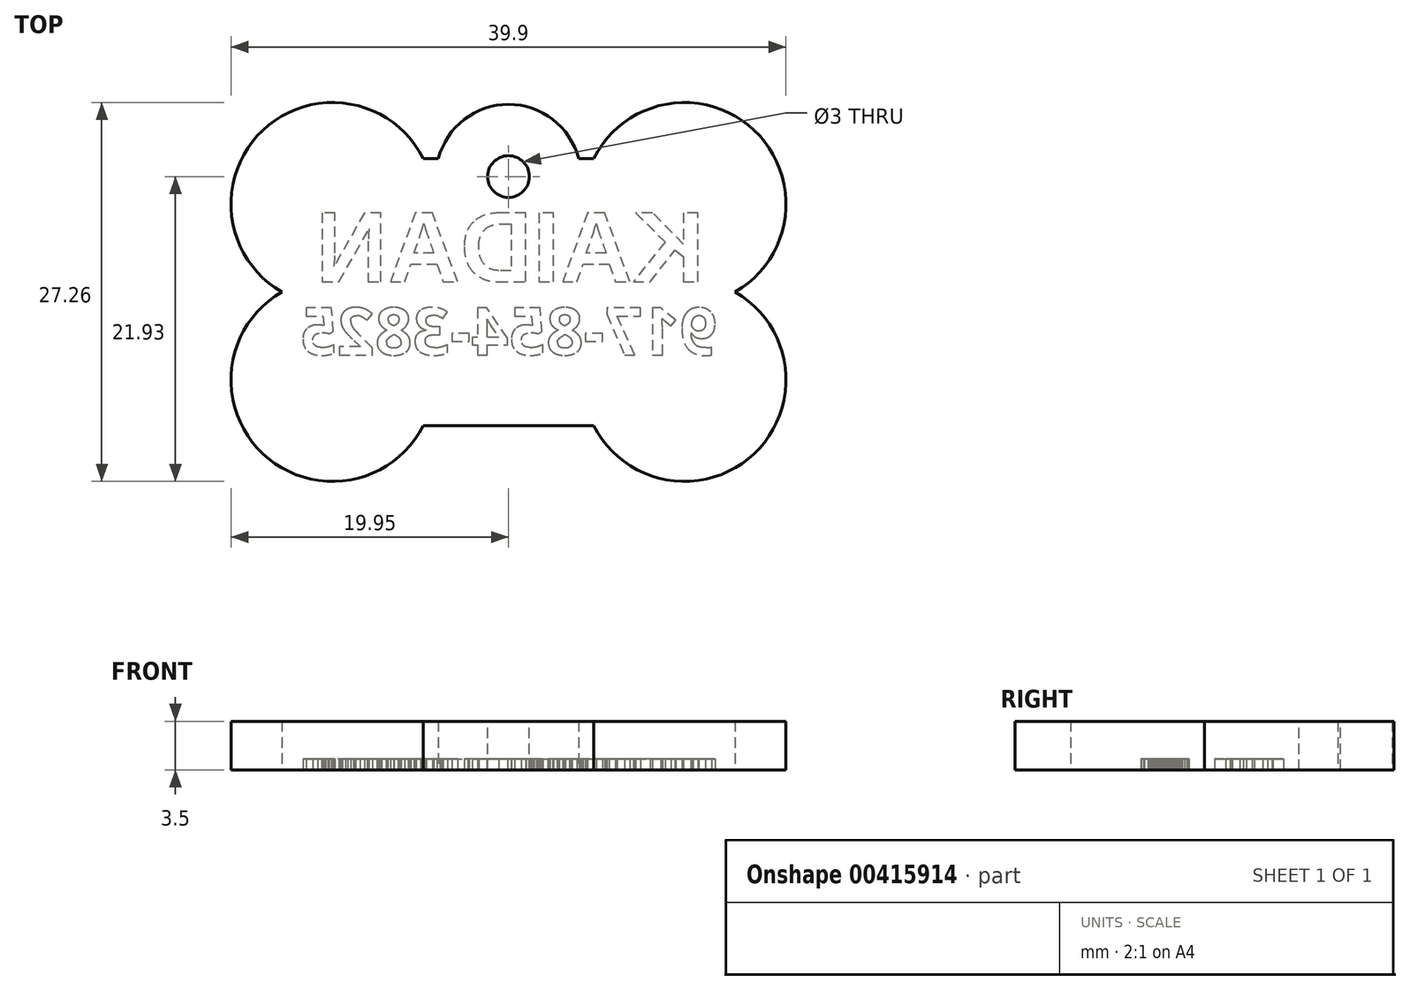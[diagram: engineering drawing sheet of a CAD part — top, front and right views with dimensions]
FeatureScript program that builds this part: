
annotation { "Feature Type Name" : "Feature", "Feature Type Description" : "" }
export const myFeature = defineFeature(function(context is Context, id is Id, definition is map)
    precondition{}
    {
        {
            var Q0;
            Q0=qCreatedBy(makeId("Top.planeOp"),FACE);
            var sketch = newSketch(context, id + "F0", { "sketchPlane" : qUnion([Q0])});
            skLineSegment(sketch, "E0.bottom", {"start": v(12.65, -6.32) * mm, "end": v(-12.65, -6.33) * mm, "construction": true});
            skLineSegment(sketch, "E0.top", {"start": v(12.65, 6.33) * mm, "end": v(-12.65, 6.32) * mm, "construction": true});
            skLineSegment(sketch, "E0.left", {"start": v(12.65, -6.32) * mm, "end": v(12.65, 6.33) * mm, "construction": true});
            skLineSegment(sketch, "E0.right", {"start": v(-12.65, -6.33) * mm, "end": v(-12.65, 6.32) * mm, "construction": true});
            skPoint(sketch, "E0.middle", {"position": v(0, 0) * mm});
            skArc(sketch, "E1", {"start": v(12.65, 0.03) * mm, "mid": v(17.85, 9.89) * mm, "end": v(6.78, 8.6) * mm});
            skArc(sketch, "E2", {"start": v(6.78, -8.6) * mm, "mid": v(17.85, -9.89) * mm, "end": v(12.65, -0.02) * mm});
            skArc(sketch, "E3", {"start": v(-12.65, -0.03) * mm, "mid": v(-17.85, -9.89) * mm, "end": v(-6.78, -8.6) * mm});
            skArc(sketch, "E4", {"start": v(-6.78, 8.6) * mm, "mid": v(-17.85, 9.89) * mm, "end": v(-12.65, 0.02) * mm});
            skLineSegment(sketch, "E5", {"start": v(-12.65, 0.02) * mm, "end": v(-12.65, -0.03) * mm});
            skLineSegment(sketch, "E6", {"start": v(12.65, -0.02) * mm, "end": v(12.65, 0.03) * mm});
            skLineSegment(sketch, "E7", {"start": v(-6.78, 8.6) * mm, "end": v(-4.19, 8.6) * mm});
            skLineSegment(sketch, "E8", {"start": v(-6.78, -8.6) * mm, "end": v(6.78, -8.6) * mm});
            skArc(sketch, "E9", {"start": v(4.19, 8.6) * mm, "mid": v(0, 12.5) * mm, "end": v(-4.19, 8.6) * mm});
            skPoint(sketch, "E10", {"position": v(0, 12.5) * mm});
            skCircle(sketch, "E11", {"center": v(0, 8.3) * mm, "radius": 1.5 * mm});
            skLineSegment(sketch, "E12.trimOffspring", {"start": v(4.19, 8.6) * mm, "end": v(6.78, 8.6) * mm});
            skLineSegment(sketch, "E13.0", {"start": v(-6.13, 9.6) * mm, "end": v(-5.03, 9.6) * mm});
            skArc(sketch, "E13.1", {"start": v(5.03, 9.6) * mm, "mid": v(0, 13.5) * mm, "end": v(-5.03, 9.6) * mm});
            skArc(sketch, "E13.2", {"start": v(-6.13, 9.6) * mm, "mid": v(-17.66, 11.63) * mm, "end": v(-16.3, 0) * mm});
            skLineSegment(sketch, "E13.3", {"start": v(5.03, 9.6) * mm, "end": v(6.13, 9.6) * mm});
            skArc(sketch, "E13.4", {"start": v(-16.3, 0) * mm, "mid": v(-17.66, -11.63) * mm, "end": v(-6.13, -9.6) * mm});
            skLineSegment(sketch, "E13.5", {"start": v(-6.13, -9.6) * mm, "end": v(6.13, -9.6) * mm});
            skArc(sketch, "E13.6", {"start": v(6.13, -9.6) * mm, "mid": v(17.66, -11.63) * mm, "end": v(16.3, 0) * mm});
            skArc(sketch, "E13.7", {"start": v(16.3, 0) * mm, "mid": v(17.66, 11.63) * mm, "end": v(6.13, 9.6) * mm});
            skSolve(sketch);
        }
        {
            var Q0;
            Q0=makeQuery(id+"F0.imprint","IMPRINT",FACE,{"disambiguationData":[TD([[makeQuery(id+"F0.imprint","IMPRINT",EDGE,{"derivedFrom":sQuery(id+"F0.wireOp",EDGE,"E1")}),-1.0]])]});
            extrude(context, id + "F1", {"entities" : qUnion([Q0]), "depth" : 2 * mm});
        }
        {
            var Q0;
            Q0=makeQuery(id+"F0.imprint","IMPRINT",FACE,{"disambiguationData":[TD([[makeQuery(id+"F0.imprint","IMPRINT",EDGE,{"derivedFrom":sQuery(id+"F0.wireOp",EDGE,"E1")}),1.0]])]});
            var Q1;
            Q1=makeQuery(id+"F0.imprint","IMPRINT",FACE,{"disambiguationData":[TD([[makeQuery(id+"F0.imprint","IMPRINT",EDGE,{"derivedFrom":sQuery(id+"F0.wireOp",EDGE,"E1")}),-1.0]])]});
            extrude(context, id + "F2", {"entities" : qUnion([Q0, Q1]), "operationType" : NewBodyOperationType.ADD, "oppositeDirection" : true, "depth" : 1.5 * mm});
        }
        {
            var Q0;
            Q0=makeQuery(id+"F2.opExtrude","CAP_FACE",FACE,{"disambiguationData":[OSD([sQuery(id+"F0.wireOp",EDGE,"E11"),sQuery(id+"F0.wireOp",EDGE,"E13.0"),sQuery(id+"F0.wireOp",EDGE,"E13.1"),sQuery(id+"F0.wireOp",EDGE,"E13.2"),sQuery(id+"F0.wireOp",EDGE,"E13.3"),sQuery(id+"F0.wireOp",EDGE,"E13.4"),sQuery(id+"F0.wireOp",EDGE,"E13.5"),sQuery(id+"F0.wireOp",EDGE,"E13.6"),sQuery(id+"F0.wireOp",EDGE,"E13.7")])],"isStart":false});
            var sketch = newSketch(context, id + "F3", { "sketchPlane" : qUnion([Q0])});
            skText(sketch, "E14", { "text": "KAIDAN", "fontName": "Arimo-Bold.ttf"});
            skText(sketch, "E15", { "text": "917-854-3825", "fontName": "OpenSans-Bold.ttf"});
            const initialGuessF3  = {"E14": [0.0141, -0.00074, -1, 0, 0.00518], "E15": [0.015, 0.00452, -1, 0, 0.0034]};
            skSetInitialGuess(sketch, initialGuessF3);
            skSolve(sketch);
        }
        {
            var Q0;
            Q0=makeQuery(id+"F3.imprint","IMPRINT",FACE,{"disambiguationData":[TD([[makeQuery(id+"F3.imprint","IMPRINT",EDGE,{"derivedFrom":sQuery(id+"F3.wireOp",EDGE,"E14.sketch_text.stroke-13")}),-1.0]])]});
            var Q1;
            Q1=makeQuery(id+"F3.imprint","IMPRINT",FACE,{"disambiguationData":[TD([[makeQuery(id+"F3.imprint","IMPRINT",EDGE,{"derivedFrom":sQuery(id+"F3.wireOp",EDGE,"E14.sketch_text.stroke-25")}),-1.0]])]});
            var Q2;
            Q2=makeQuery(id+"F3.imprint","IMPRINT",FACE,{"disambiguationData":[TD([[makeQuery(id+"F3.imprint","IMPRINT",EDGE,{"derivedFrom":sQuery(id+"F3.wireOp",EDGE,"E14.sketch_text.stroke-29")}),-1.0]])]});
            var Q3;
            Q3=makeQuery(id+"F3.imprint","IMPRINT",FACE,{"disambiguationData":[TD([[makeQuery(id+"F3.imprint","IMPRINT",EDGE,{"derivedFrom":sQuery(id+"F3.wireOp",EDGE,"E14.sketch_text.stroke-41")}),-1.0]])]});
            var Q4;
            Q4=makeQuery(id+"F3.imprint","IMPRINT",FACE,{"disambiguationData":[TD([[makeQuery(id+"F3.imprint","IMPRINT",EDGE,{"derivedFrom":sQuery(id+"F3.wireOp",EDGE,"E14.sketch_text.stroke-53")}),-1.0]])]});
            var Q5;
            Q5=makeQuery(id+"F3.imprint","IMPRINT",FACE,{"disambiguationData":[TD([[makeQuery(id+"F3.imprint","IMPRINT",EDGE,{"derivedFrom":sQuery(id+"F3.wireOp",EDGE,"E15.sketch_text.stroke-0")}),-1.0]])]});
            var Q6;
            Q6=makeQuery(id+"F3.imprint","IMPRINT",FACE,{"disambiguationData":[TD([[makeQuery(id+"F3.imprint","IMPRINT",EDGE,{"derivedFrom":sQuery(id+"F3.wireOp",EDGE,"E15.sketch_text.stroke-26")}),-1.0]])]});
            var Q7;
            Q7=makeQuery(id+"F3.imprint","IMPRINT",FACE,{"disambiguationData":[TD([[makeQuery(id+"F3.imprint","IMPRINT",EDGE,{"derivedFrom":sQuery(id+"F3.wireOp",EDGE,"E15.sketch_text.stroke-36")}),-1.0]])]});
            var Q8;
            Q8=makeQuery(id+"F3.imprint","IMPRINT",FACE,{"disambiguationData":[TD([[makeQuery(id+"F3.imprint","IMPRINT",EDGE,{"derivedFrom":sQuery(id+"F3.wireOp",EDGE,"E15.sketch_text.stroke-43")}),-1.0]])]});
            var Q9;
            Q9=makeQuery(id+"F3.imprint","IMPRINT",FACE,{"disambiguationData":[TD([[makeQuery(id+"F3.imprint","IMPRINT",EDGE,{"derivedFrom":sQuery(id+"F3.wireOp",EDGE,"E15.sketch_text.stroke-47")}),-1.0]])]});
            var Q10;
            Q10=makeQuery(id+"F3.imprint","IMPRINT",FACE,{"disambiguationData":[TD([[makeQuery(id+"F3.imprint","IMPRINT",EDGE,{"derivedFrom":sQuery(id+"F3.wireOp",EDGE,"E15.sketch_text.stroke-78")}),-1.0]])]});
            var Q11;
            Q11=makeQuery(id+"F3.imprint","IMPRINT",FACE,{"disambiguationData":[TD([[makeQuery(id+"F3.imprint","IMPRINT",EDGE,{"derivedFrom":sQuery(id+"F3.wireOp",EDGE,"E15.sketch_text.stroke-98")}),-1.0]])]});
            var Q12;
            Q12=makeQuery(id+"F3.imprint","IMPRINT",FACE,{"disambiguationData":[TD([[makeQuery(id+"F3.imprint","IMPRINT",EDGE,{"derivedFrom":sQuery(id+"F3.wireOp",EDGE,"E15.sketch_text.stroke-116")}),-1.0]])]});
            var Q13;
            Q13=makeQuery(id+"F3.imprint","IMPRINT",FACE,{"disambiguationData":[TD([[makeQuery(id+"F3.imprint","IMPRINT",EDGE,{"derivedFrom":sQuery(id+"F3.wireOp",EDGE,"E15.sketch_text.stroke-120")}),-1.0]])]});
            var Q14;
            Q14=makeQuery(id+"F3.imprint","IMPRINT",FACE,{"disambiguationData":[TD([[makeQuery(id+"F3.imprint","IMPRINT",EDGE,{"derivedFrom":sQuery(id+"F3.wireOp",EDGE,"E15.sketch_text.stroke-147")}),-1.0]])]});
            var Q15;
            Q15=makeQuery(id+"F3.imprint","IMPRINT",FACE,{"disambiguationData":[TD([[makeQuery(id+"F3.imprint","IMPRINT",EDGE,{"derivedFrom":sQuery(id+"F3.wireOp",EDGE,"E15.sketch_text.stroke-178")}),-1.0]])]});
            var Q16;
            Q16=makeQuery(id+"F3.imprint","IMPRINT",FACE,{"disambiguationData":[TD([[makeQuery(id+"F3.imprint","IMPRINT",EDGE,{"derivedFrom":sQuery(id+"F3.wireOp",EDGE,"E15.sketch_text.stroke-202")}),-1.0]])]});
            var Q17;
            Q17=makeQuery(id+"F3.imprint","IMPRINT",FACE,{"disambiguationData":[TD([[makeQuery(id+"F3.imprint","IMPRINT",EDGE,{"derivedFrom":sQuery(id+"F3.wireOp",EDGE,"E14.sketch_text.stroke-61")}),-1.0]])]});
            var Q18;
            Q18=makeQuery(id+"F3.imprint","IMPRINT",FACE,{"disambiguationData":[TD([[makeQuery(id+"F3.imprint","IMPRINT",EDGE,{"derivedFrom":sQuery(id+"F3.wireOp",EDGE,"E14.sketch_text.stroke-0")}),-1.0]])]});
            extrude(context, id + "F4", {"entities" : qUnion([Q0, Q1, Q2, Q3, Q4, Q5, Q6, Q7, Q8, Q9, Q10, Q11, Q12, Q13, Q14, Q15, Q16, Q17, Q18]), "operationType" : NewBodyOperationType.REMOVE, "oppositeDirection" : true, "depth" : .8 * mm});
        }
        {
            var Q0;
            Q0=makeQuery(id+"F2.opExtrude","CAP_FACE",FACE,{"disambiguationData":[OSD([sQuery(id+"F0.wireOp",EDGE,"E11"),sQuery(id+"F0.wireOp",EDGE,"E13.0"),sQuery(id+"F0.wireOp",EDGE,"E13.1"),sQuery(id+"F0.wireOp",EDGE,"E13.2"),sQuery(id+"F0.wireOp",EDGE,"E13.3"),sQuery(id+"F0.wireOp",EDGE,"E13.4"),sQuery(id+"F0.wireOp",EDGE,"E13.5"),sQuery(id+"F0.wireOp",EDGE,"E13.6"),sQuery(id+"F0.wireOp",EDGE,"E13.7")])],"isStart":true});
            var Q1;
            {var subQ0=sQuery(id+"F0.wireOp",EDGE,"E13.4");var subQ1=sQuery(id+"F0.wireOp",EDGE,"E13.3");var subQ2=sQuery(id+"F0.wireOp",EDGE,"E13.2");var subQ3=sQuery(id+"F0.wireOp",EDGE,"E13.0");var subQ4=sQuery(id+"F0.wireOp",EDGE,"E13.5");var subQ5=sQuery(id+"F0.wireOp",EDGE,"E13.7");var subQ6=sQuery(id+"F0.wireOp",EDGE,"E13.6");var subQ7=sQuery(id+"F0.wireOp",EDGE,"E13.1");var subQ8=sQuery(id+"F0.wireOp",EDGE,"E11");Q1=makeQuery(id+"F4.boolean.opBoolean","SPLIT",FACE,{"disambiguationData":[TD([makeQuery(id+"F1.opExtrude","SWEPT_FACE",FACE,{"disambiguationData":[OSD([subQ3])]})])],"derivedFrom":makeQuery(id+"F2.opExtrude","CAP_FACE",FACE,{"disambiguationData":[OSD([subQ8,subQ3,subQ7,subQ2,subQ1,subQ0,subQ4,subQ6,subQ5])],"isStart":false})});}
            extrude(context, id + "F5", {"entities" : qUnion([Q0, Q1]), "operationType" : NewBodyOperationType.ADD, "depth" : 2 * mm});
        }
    });
